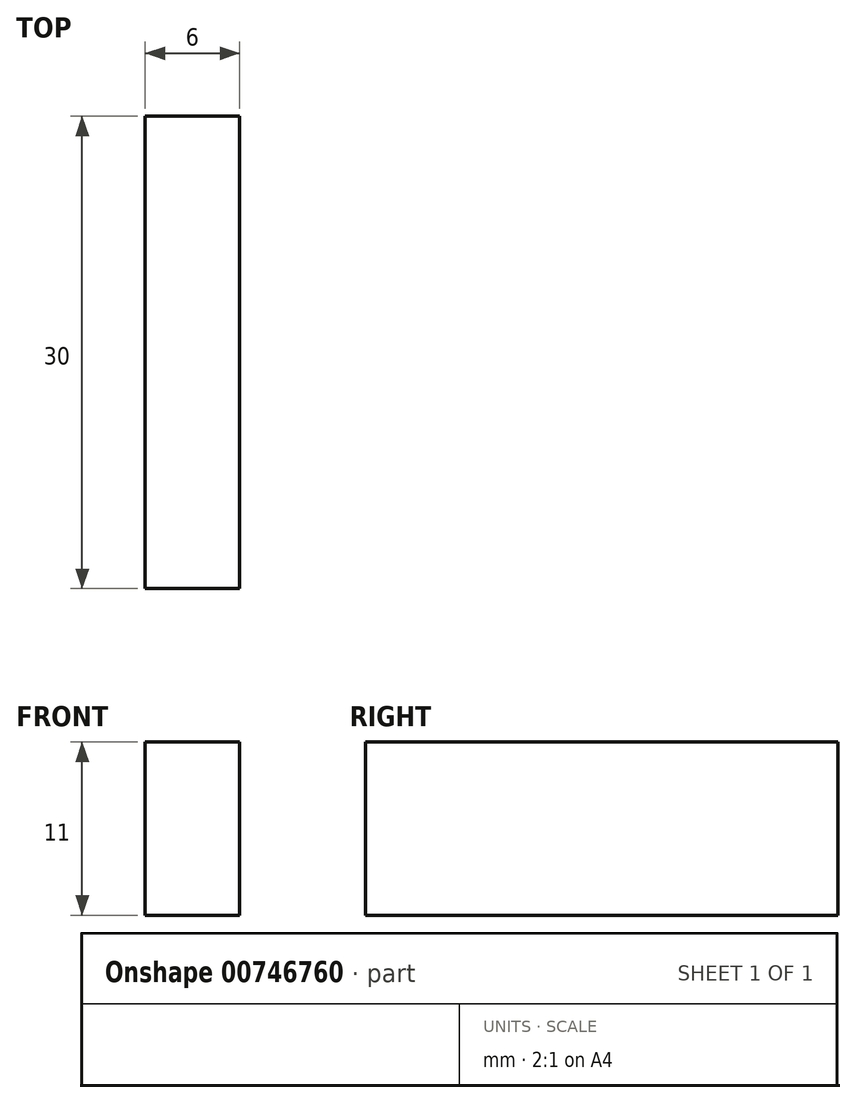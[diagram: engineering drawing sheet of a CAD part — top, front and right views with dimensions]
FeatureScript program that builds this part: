
annotation { "Feature Type Name" : "Feature", "Feature Type Description" : "" }
export const myFeature = defineFeature(function(context is Context, id is Id, definition is map)
    precondition{}
    {
        {
            var Q0;
            Q0=qCreatedBy(makeId("Top.planeOp"),FACE);
            var sketch = newSketch(context, id + "F0", { "sketchPlane" : qUnion([Q0])});
            skLineSegment(sketch, "E0.bottom", {"start": v(-6, 19.87) * mm, "end": v(0, 19.87) * mm});
            skLineSegment(sketch, "E0.top", {"start": v(-6, -10.13) * mm, "end": v(0, -10.13) * mm});
            skLineSegment(sketch, "E0.left", {"start": v(-6, 19.87) * mm, "end": v(-6, -10.13) * mm});
            skLineSegment(sketch, "E0.right", {"start": v(0, 19.87) * mm, "end": v(0, -10.13) * mm});
            skSolve(sketch);
        }
        {
            var Q0;
            Q0=makeQuery(id+"F0.imprint","IMPRINT",FACE,{"disambiguationData":[TD([[makeQuery(id+"F0.imprint","IMPRINT",EDGE,{"derivedFrom":sQuery(id+"F0.wireOp",EDGE,"E0.bottom")}),-1.0]])]});
            extrude(context, id + "F1", {"entities" : qUnion([Q0]), "depth" : 11 * mm, "offsetDistance" : 25 * mm});
        }
    });
